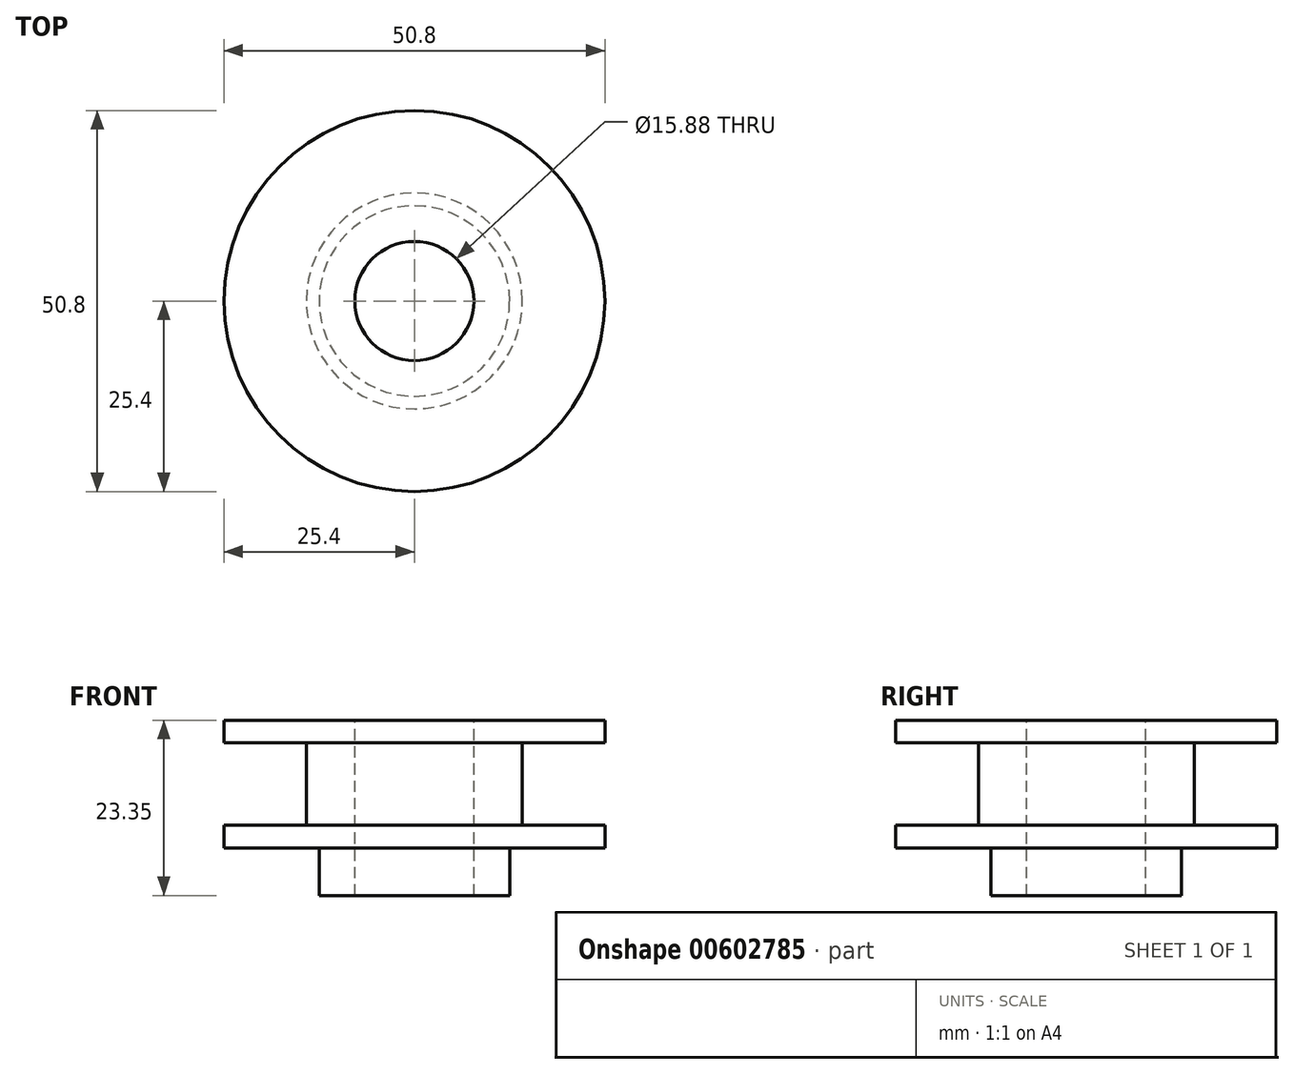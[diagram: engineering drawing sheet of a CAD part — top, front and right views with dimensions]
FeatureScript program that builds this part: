
annotation { "Feature Type Name" : "Feature", "Feature Type Description" : "" }
export const myFeature = defineFeature(function(context is Context, id is Id, definition is map)
    precondition{}
    {
        {
            var Q0;
            Q0=qCreatedBy(makeId("Right.planeOp"),FACE);
            var sketch = newSketch(context, id + "F0", { "sketchPlane" : qUnion([Q0])});
            skLineSegment(sketch, "E0", {"start": v(0, 0) * mm, "end": v(25.4, 0) * mm});
            skLineSegment(sketch, "E1", {"start": v(25.4, 0) * mm, "end": v(25.4, 3) * mm});
            skLineSegment(sketch, "E2", {"start": v(25.4, 3) * mm, "end": v(14.4, 3) * mm});
            skLineSegment(sketch, "E3", {"start": v(14.4, 3) * mm, "end": v(14.4, 14) * mm});
            skLineSegment(sketch, "E4", {"start": v(14.4, 14) * mm, "end": v(25.4, 14) * mm});
            skLineSegment(sketch, "E5", {"start": v(25.4, 14) * mm, "end": v(25.4, 17) * mm});
            skLineSegment(sketch, "E6", {"start": v(25.4, 17) * mm, "end": v(0, 17) * mm});
            skLineSegment(sketch, "E7", {"start": v(0, 17) * mm, "end": v(0, 0) * mm});
            skSolve(sketch);
        }
        {
            var Q0;
            Q0=makeQuery(id+"F0.imprint","IMPRINT",FACE,{"disambiguationData":[TD([[makeQuery(id+"F0.imprint","IMPRINT",EDGE,{"derivedFrom":sQuery(id+"F0.wireOp",EDGE,"E0")}),1.0]])]});
            var Q1;
            Q1=sQuery(id+"F0.wireOp",EDGE,"E7");
            revolve(context, id + "F1", {"entities" : qUnion([Q0]), "axis" : qUnion([Q1]), "revolveType" : RevolveType.FULL});
        }
        {
            var Q0;
            Q0=makeQuery(id+"F1.opRevolve","SWEPT_FACE",FACE,{"disambiguationData":[OSD([sQuery(id+"F0.wireOp",EDGE,"E6")])]});
            var sketch = newSketch(context, id + "F2", { "sketchPlane" : qUnion([Q0])});
            skCircle(sketch, "E8", {"center": v(0, 0) * mm, "radius": 7.94 * mm});
            skSolve(sketch);
        }
        {
            var Q0;
            Q0 = qSketchRegion(id + "F2", true);
            extrude(context, id + "F3", {"entities" : qUnion([Q0]), "operationType" : NewBodyOperationType.REMOVE, "oppositeDirection" : true, "depth" : 25.4 * mm, "offsetDistance" : 25.4 * mm});
        }
        {
            var Q0;
            Q0=makeQuery(id+"F1.opRevolve","SWEPT_FACE",FACE,{"disambiguationData":[OSD([sQuery(id+"F0.wireOp",EDGE,"E0")])]});
            var sketch = newSketch(context, id + "F4", { "sketchPlane" : qUnion([Q0])});
            skCircle(sketch, "E9", {"center": v(0, 0) * mm, "radius": 7.94 * mm});
            skCircle(sketch, "E10", {"center": v(0, 0) * mm, "radius": 12.7 * mm});
            skSolve(sketch);
        }
        {
            var Q0;
            Q0 = qSketchRegion(id + "F4", true);
            extrude(context, id + "F5", {"entities" : qUnion([Q0]), "operationType" : NewBodyOperationType.ADD, "depth" : 6.35 * mm, "offsetDistance" : 25.4 * mm});
        }
    });
